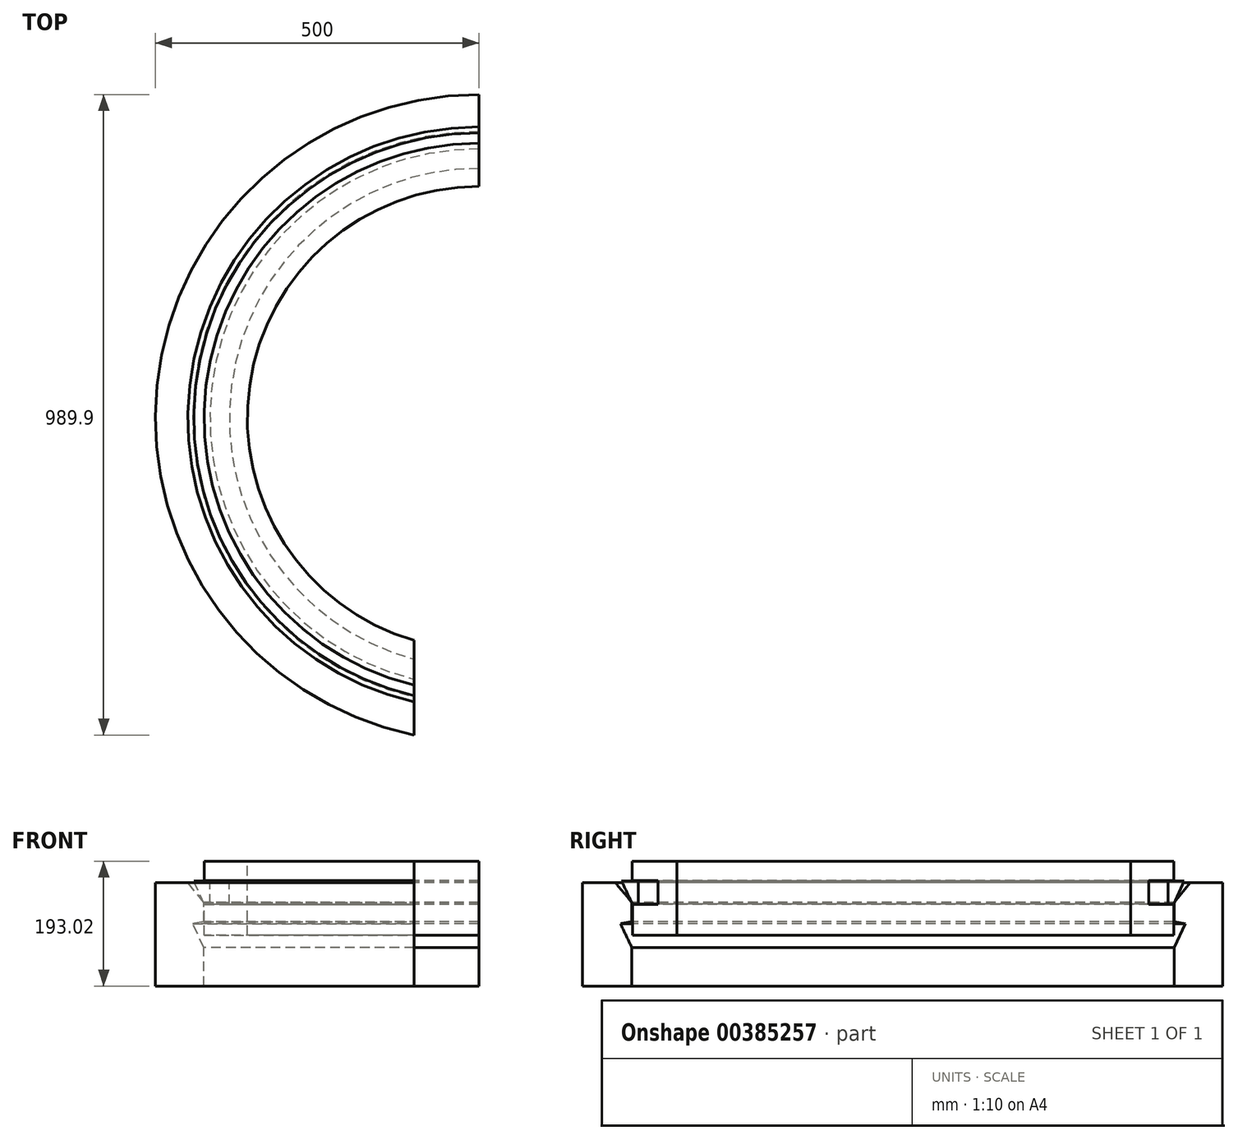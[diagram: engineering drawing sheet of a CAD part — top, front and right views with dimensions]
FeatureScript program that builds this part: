
annotation { "Feature Type Name" : "Feature", "Feature Type Description" : "" }
export const myFeature = defineFeature(function(context is Context, id is Id, definition is map)
    precondition{}
    {
        {
            var Q0;
            Q0=qCreatedBy(makeId("Front.planeOp"),FACE);
            var sketch = newSketch(context, id + "F0", { "sketchPlane" : qUnion([Q0])});
            skLineSegment(sketch, "E0", {"start": v(0, 509.7) * mm, "end": v(0, -191.27) * mm, "construction": true});
            skLineSegment(sketch, "E1", {"start": v(-500, 274.96) * mm, "end": v(-500, 115.33) * mm});
            skLineSegment(sketch, "E2", {"start": v(-500, 274.96) * mm, "end": v(-450, 274.96) * mm});
            skLineSegment(sketch, "E3", {"start": v(-450, 274.96) * mm, "end": v(-425.32, 244.76) * mm});
            skLineSegment(sketch, "E4", {"start": v(-425.32, 244.76) * mm, "end": v(-425.32, 214.81) * mm});
            skLineSegment(sketch, "E5", {"start": v(-442.37, 211.66) * mm, "end": v(-425.32, 174.8) * mm});
            skLineSegment(sketch, "E6", {"start": v(-425.32, 174.8) * mm, "end": v(-425.32, 115.33) * mm});
            skLineSegment(sketch, "E7.0", {"start": v(-440.8, 210.66) * mm, "end": v(-424.41, 175.23) * mm});
            skLineSegment(sketch, "E7.1", {"start": v(-425.32, 210.66) * mm, "end": v(-440.8, 210.66) * mm});
            skLineSegment(sketch, "E8", {"start": v(-425.32, 210.66) * mm, "end": v(-415.8, 210.66) * mm});
            skLineSegment(sketch, "E9", {"start": v(-415.8, 210.66) * mm, "end": v(-415.8, 175.23) * mm});
            skLineSegment(sketch, "E10", {"start": v(-415.8, 175.23) * mm, "end": v(-424.41, 175.23) * mm});
            skLineSegment(sketch, "E11.0", {"start": v(-424.82, 211.16) * mm, "end": v(-414.4, 211.16) * mm});
            skLineSegment(sketch, "E12.0", {"start": v(-424.82, 241.35) * mm, "end": v(-424.82, 211.16) * mm});
            skLineSegment(sketch, "E13", {"start": v(-414.4, 211.16) * mm, "end": v(-385.8, 211.16) * mm});
            skLineSegment(sketch, "E14", {"start": v(-385.8, 211.16) * mm, "end": v(-385.8, 174.73) * mm});
            skLineSegment(sketch, "E15.0", {"start": v(-385.8, 174.73) * mm, "end": v(-424.41, 174.73) * mm});
            skLineSegment(sketch, "E16", {"start": v(-424.41, 174.73) * mm, "end": v(-424.41, 126.88) * mm});
            skLineSegment(sketch, "E17", {"start": v(-424.41, 126.88) * mm, "end": v(-358.03, 126.88) * mm});
            skLineSegment(sketch, "E18", {"start": v(-358.03, 126.88) * mm, "end": v(-358.03, 241.35) * mm});
            skLineSegment(sketch, "E19", {"start": v(-358.03, 241.35) * mm, "end": v(-424.82, 241.35) * mm});
            skLineSegment(sketch, "E20", {"start": v(-500, 115.33) * mm, "end": v(-425.32, 115.33) * mm});
            skLineSegment(sketch, "E21", {"start": v(-442.37, 211.66) * mm, "end": v(-425.32, 214.81) * mm});
            skPoint(sketch, "E22.orphan", {"position": v(-425.32, 211.66) * mm});
            skSolve(sketch);
        }
        {
            var Q0;
            Q0 = qSketchRegion(id + "F0", true);
            var Q1;
            Q1=sQuery(id+"F0.wireOp",EDGE,"E0");
            revolve(context, id + "F1", {"entities" : qUnion([Q0]), "axis" : qUnion([Q1]), "revolveType" : RevolveType.FULL});
        }
        {
            var Q0;
            Q0=qCreatedBy(makeId("Top.planeOp"),FACE);
            var sketch = newSketch(context, id + "F2", { "sketchPlane" : qUnion([Q0])});
            skLineSegment(sketch, "E23.bottom", {"start": v(-100, -262.3) * mm, "end": v(100, -262.3) * mm});
            skLineSegment(sketch, "E23.top", {"start": v(-100, -543.33) * mm, "end": v(100, -543.33) * mm});
            skLineSegment(sketch, "E23.left", {"start": v(-100, -262.3) * mm, "end": v(-100, -543.33) * mm});
            skLineSegment(sketch, "E23.right", {"start": v(100, -262.3) * mm, "end": v(100, -543.33) * mm});
            skSolve(sketch);
        }
        {
            var Q0;
            Q0=makeQuery(id+"F2.imprint","IMPRINT",FACE,{"disambiguationData":[TD([[makeQuery(id+"F2.imprint","IMPRINT",EDGE,{"derivedFrom":sQuery(id+"F2.wireOp",EDGE,"E23.bottom")}),-1.0]])]});
            extrude(context, id + "F3", {"entities" : qUnion([Q0]), "operationType" : NewBodyOperationType.REMOVE, "endBound" : BoundingType.THROUGH_ALL, "depth" : 25 * mm});
        }
        {
            var Q0;
            Q0=qCreatedBy(makeId("Top.planeOp"),FACE);
            var sketch = newSketch(context, id + "F4", { "sketchPlane" : qUnion([Q0])});
            skLineSegment(sketch, "E24.bottom", {"start": v(0, 559.66) * mm, "end": v(569.53, 559.66) * mm});
            skLineSegment(sketch, "E24.top", {"start": v(0, -619.77) * mm, "end": v(569.53, -619.77) * mm});
            skLineSegment(sketch, "E24.left", {"start": v(0, 559.66) * mm, "end": v(0, -619.77) * mm});
            skLineSegment(sketch, "E24.right", {"start": v(569.53, 559.66) * mm, "end": v(569.53, -619.77) * mm});
            skSolve(sketch);
        }
        {
            var Q0;
            Q0=makeQuery(id+"F4.imprint","IMPRINT",FACE,{"disambiguationData":[TD([[makeQuery(id+"F4.imprint","IMPRINT",EDGE,{"derivedFrom":sQuery(id+"F4.wireOp",EDGE,"E24.bottom")}),-1.0]])]});
            extrude(context, id + "F5", {"entities" : qUnion([Q0]), "operationType" : NewBodyOperationType.REMOVE, "endBound" : BoundingType.THROUGH_ALL, "depth" : 25 * mm});
        }
        {
            var Q0;
            Q0=makeQuery(id+"F1.opRevolve","SWEPT_BODY",BODY,{"disambiguationData":[OSD([sQuery(id+"F0.wireOp",EDGE,"E11.0"),sQuery(id+"F0.wireOp",EDGE,"E12.0"),sQuery(id+"F0.wireOp",EDGE,"E13"),sQuery(id+"F0.wireOp",EDGE,"E14"),sQuery(id+"F0.wireOp",EDGE,"E15.0"),sQuery(id+"F0.wireOp",EDGE,"E16"),sQuery(id+"F0.wireOp",EDGE,"E17"),sQuery(id+"F0.wireOp",EDGE,"E18"),sQuery(id+"F0.wireOp",EDGE,"E19")])]});
            var Q1;
            Q1=makeQuery(id+"F1.opRevolve","SWEPT_BODY",BODY,{"disambiguationData":[OSD([sQuery(id+"F0.wireOp",EDGE,"E7.0"),sQuery(id+"F0.wireOp",EDGE,"E7.1"),sQuery(id+"F0.wireOp",EDGE,"E8"),sQuery(id+"F0.wireOp",EDGE,"E9"),sQuery(id+"F0.wireOp",EDGE,"E10")])]});
            transform(context, id + "F6", {"entities" : qUnion([Q0, Q1]), "transformType" : TransformType.TRANSLATION_3D, "dx" : 0 * mm, "dy" : 0 * mm, "dz" : 67 * mm, "makeCopy" : false});
        }
    });
